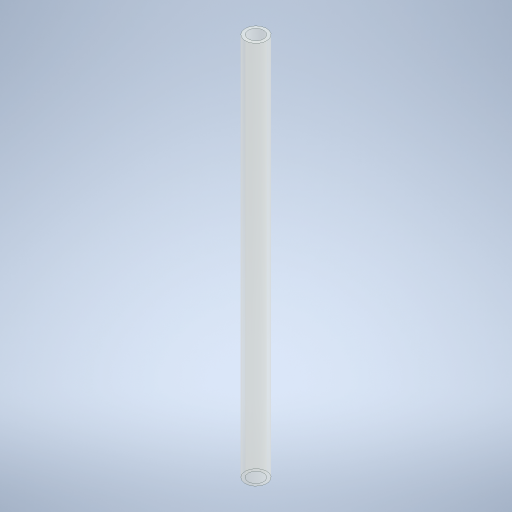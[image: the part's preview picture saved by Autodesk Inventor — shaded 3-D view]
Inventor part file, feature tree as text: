
AUTODESK INVENTOR PART (.ipt)
format: ipt  version: 2023 (Build 270158000, 158)  size: 246,272 bytes
history: native  units: mm
features: extrude x1, sketch x1
ambient origin geometry x8: Origin, YZ Plane, XZ Plane, XY Plane, X Axis, Y Axis, Z Axis, Center Point
bodies: Solid1 (feature_tree)
feature tree (2):
  extrude  "Extrusion1"  Depth=125.0mm
  sketch  "Sketch1"  dims[d0=7.0mm d1=1.0mm d2=125.0mm d3=0.0mm]
